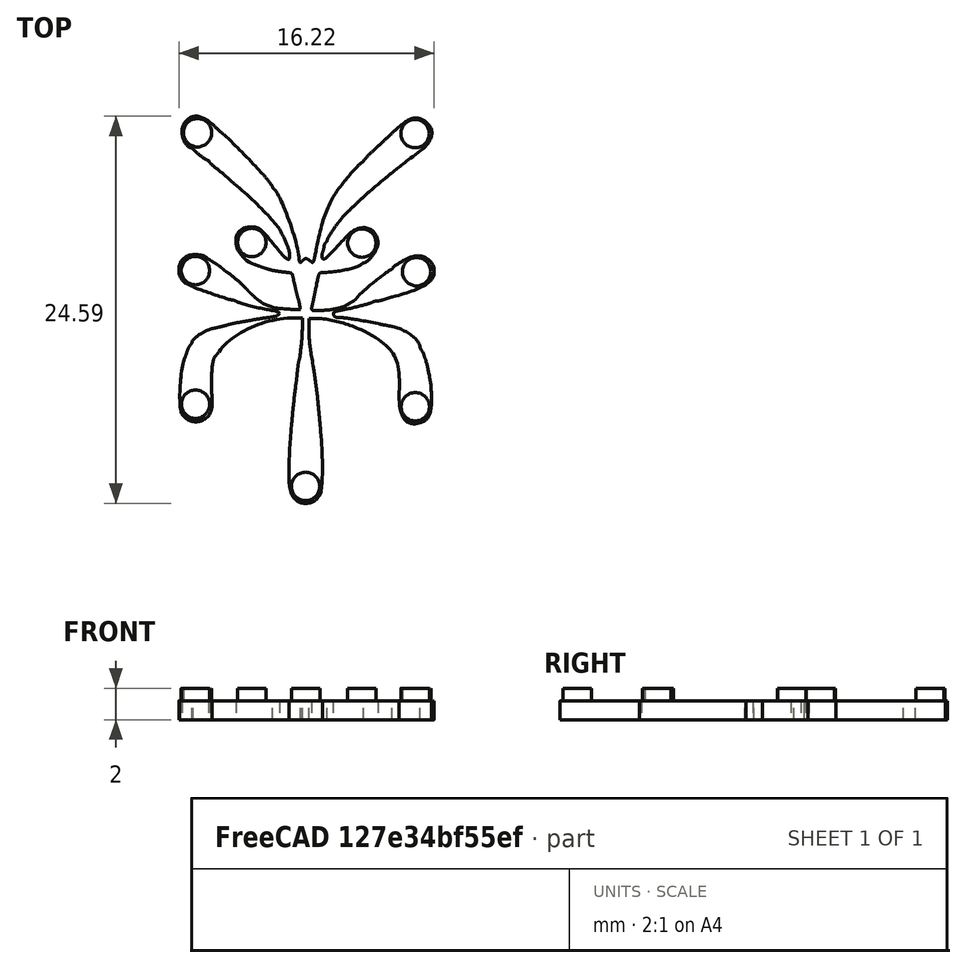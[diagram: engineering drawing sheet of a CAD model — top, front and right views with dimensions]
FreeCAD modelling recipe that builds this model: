
FCSTD DOCUMENT  (FreeCAD 0.20R29177 (Git))
Label: frexten
License: All rights reserved
LicenseURL: http://en.wikipedia.org/wiki/All_rights_reserved
objects: Part::FeaturePython×7, Sketcher::SketchObject×2, PartDesign::Pad×2, App::DocumentObjectGroupPython×2, Part::Feature×1, PartDesign::Body×1, App::MaterialObjectPython×1
note: 15 computed .brp shape members not serialized (recipe doc carries the construction recipe); baked Part::Feature solids carry a one-line shape summary decoded from their .brp

FEATURE [Part::Feature] path1527001
  shape: bbox 72.27 x 108.1 x 2e-07 mm, 1 faces, 0 solids (baked)
FEATURE [Part::FeaturePython] Clone  label="path1527002"  # Draft clone (typed FeaturePython)
  AttacherType = Attacher::AttachEngine3D
  Fuse = false
  Objects = -> [path1527001]
  Placement = pos=(26.6865,-58.6467,0) rot=(0,0,1;0rad)
  Scale = (0.23,0.23,0.23)
FEATURE [Sketcher::SketchObject] Sketch
  FullyConstrained = false
  sketch-geometry (125):
    g0: BSplineCurve PolesCount=4 KnotsCount=2 Degree=3 IsPeriodic=0
    g1: BSplineCurve PolesCount=4 KnotsCount=2 Degree=3 IsPeriodic=0
    g2: BSplineCurve PolesCount=4 KnotsCount=2 Degree=3 IsPeriodic=0
    g3: BSplineCurve PolesCount=4 KnotsCount=2 Degree=3 IsPeriodic=0
    g4: BSplineCurve PolesCount=4 KnotsCount=2 Degree=3 IsPeriodic=0
    g5: BSplineCurve PolesCount=4 KnotsCount=2 Degree=3 IsPeriodic=0
    g6: BSplineCurve PolesCount=2 KnotsCount=2 Degree=1 IsPeriodic=0
    g7: BSplineCurve PolesCount=2 KnotsCount=2 Degree=1 IsPeriodic=0
    g8: BSplineCurve PolesCount=4 KnotsCount=2 Degree=3 IsPeriodic=0
    g9: BSplineCurve PolesCount=4 KnotsCount=2 Degree=3 IsPeriodic=0
    g10: BSplineCurve PolesCount=4 KnotsCount=2 Degree=3 IsPeriodic=0
    g11: BSplineCurve PolesCount=4 KnotsCount=2 Degree=3 IsPeriodic=0
    g12: BSplineCurve PolesCount=4 KnotsCount=2 Degree=3 IsPeriodic=0
    g13: BSplineCurve PolesCount=4 KnotsCount=2 Degree=3 IsPeriodic=0
    g14: BSplineCurve PolesCount=4 KnotsCount=2 Degree=3 IsPeriodic=0
    g15: BSplineCurve PolesCount=4 KnotsCount=2 Degree=3 IsPeriodic=0
    g16: BSplineCurve PolesCount=4 KnotsCount=2 Degree=3 IsPeriodic=0
    g17: BSplineCurve PolesCount=4 KnotsCount=2 Degree=3 IsPeriodic=0
    g18: BSplineCurve PolesCount=4 KnotsCount=2 Degree=3 IsPeriodic=0
    g19: BSplineCurve PolesCount=4 KnotsCount=2 Degree=3 IsPeriodic=0
    g20: BSplineCurve PolesCount=4 KnotsCount=2 Degree=3 IsPeriodic=0
    g21: BSplineCurve PolesCount=4 KnotsCount=2 Degree=3 IsPeriodic=0
    g22: BSplineCurve PolesCount=4 KnotsCount=2 Degree=3 IsPeriodic=0
    g23: BSplineCurve PolesCount=4 KnotsCount=2 Degree=3 IsPeriodic=0
    g24: BSplineCurve PolesCount=4 KnotsCount=2 Degree=3 IsPeriodic=0
    g25: BSplineCurve PolesCount=4 KnotsCount=2 Degree=3 IsPeriodic=0
    g26: BSplineCurve PolesCount=4 KnotsCount=2 Degree=3 IsPeriodic=0
    g27: BSplineCurve PolesCount=4 KnotsCount=2 Degree=3 IsPeriodic=0
    g28: BSplineCurve PolesCount=4 KnotsCount=2 Degree=3 IsPeriodic=0
    g29: BSplineCurve PolesCount=4 KnotsCount=2 Degree=3 IsPeriodic=0
    g30: BSplineCurve PolesCount=4 KnotsCount=2 Degree=3 IsPeriodic=0
    g31: BSplineCurve PolesCount=4 KnotsCount=2 Degree=3 IsPeriodic=0
    g32: BSplineCurve PolesCount=4 KnotsCount=2 Degree=3 IsPeriodic=0
    g33: BSplineCurve PolesCount=4 KnotsCount=2 Degree=3 IsPeriodic=0
    g34: BSplineCurve PolesCount=4 KnotsCount=2 Degree=3 IsPeriodic=0
    g35: BSplineCurve PolesCount=4 KnotsCount=2 Degree=3 IsPeriodic=0
    g36: BSplineCurve PolesCount=4 KnotsCount=2 Degree=3 IsPeriodic=0
    g37: BSplineCurve PolesCount=4 KnotsCount=2 Degree=3 IsPeriodic=0
    g38: BSplineCurve PolesCount=4 KnotsCount=2 Degree=3 IsPeriodic=0
    g39: BSplineCurve PolesCount=4 KnotsCount=2 Degree=3 IsPeriodic=0
    g40: BSplineCurve PolesCount=4 KnotsCount=2 Degree=3 IsPeriodic=0
    g41: BSplineCurve PolesCount=4 KnotsCount=2 Degree=3 IsPeriodic=0
    g42: BSplineCurve PolesCount=4 KnotsCount=2 Degree=3 IsPeriodic=0
    g43: BSplineCurve PolesCount=4 KnotsCount=2 Degree=3 IsPeriodic=0
    g44: BSplineCurve PolesCount=4 KnotsCount=2 Degree=3 IsPeriodic=0
    g45: BSplineCurve PolesCount=4 KnotsCount=2 Degree=3 IsPeriodic=0
    g46: BSplineCurve PolesCount=4 KnotsCount=2 Degree=3 IsPeriodic=0
    g47: BSplineCurve PolesCount=4 KnotsCount=2 Degree=3 IsPeriodic=0
    g48: BSplineCurve PolesCount=4 KnotsCount=2 Degree=3 IsPeriodic=0
    g49: BSplineCurve PolesCount=4 KnotsCount=2 Degree=3 IsPeriodic=0
    g50: BSplineCurve PolesCount=4 KnotsCount=2 Degree=3 IsPeriodic=0
    g51: BSplineCurve PolesCount=4 KnotsCount=2 Degree=3 IsPeriodic=0
    g52: BSplineCurve PolesCount=4 KnotsCount=2 Degree=3 IsPeriodic=0
    g53: BSplineCurve PolesCount=4 KnotsCount=2 Degree=3 IsPeriodic=0
    g54: BSplineCurve PolesCount=4 KnotsCount=2 Degree=3 IsPeriodic=0
    g55: BSplineCurve PolesCount=4 KnotsCount=2 Degree=3 IsPeriodic=0
    g56: BSplineCurve PolesCount=4 KnotsCount=2 Degree=3 IsPeriodic=0
    g57: BSplineCurve PolesCount=4 KnotsCount=2 Degree=3 IsPeriodic=0
    g58: BSplineCurve PolesCount=4 KnotsCount=2 Degree=3 IsPeriodic=0
    g59: BSplineCurve PolesCount=4 KnotsCount=2 Degree=3 IsPeriodic=0
    g60: BSplineCurve PolesCount=4 KnotsCount=2 Degree=3 IsPeriodic=0
    g61: BSplineCurve PolesCount=4 KnotsCount=2 Degree=3 IsPeriodic=0
    g62: BSplineCurve PolesCount=4 KnotsCount=2 Degree=3 IsPeriodic=0
    g63: BSplineCurve PolesCount=4 KnotsCount=2 Degree=3 IsPeriodic=0
    g64: BSplineCurve PolesCount=4 KnotsCount=2 Degree=3 IsPeriodic=0
    g65: BSplineCurve PolesCount=4 KnotsCount=2 Degree=3 IsPeriodic=0
    g66: BSplineCurve PolesCount=4 KnotsCount=2 Degree=3 IsPeriodic=0
    g67: BSplineCurve PolesCount=4 KnotsCount=2 Degree=3 IsPeriodic=0
    g68: BSplineCurve PolesCount=4 KnotsCount=2 Degree=3 IsPeriodic=0
    g69: BSplineCurve PolesCount=4 KnotsCount=2 Degree=3 IsPeriodic=0
    g70: BSplineCurve PolesCount=4 KnotsCount=2 Degree=3 IsPeriodic=0
    g71: BSplineCurve PolesCount=4 KnotsCount=2 Degree=3 IsPeriodic=0
    g72: BSplineCurve PolesCount=4 KnotsCount=2 Degree=3 IsPeriodic=0
    g73: BSplineCurve PolesCount=4 KnotsCount=2 Degree=3 IsPeriodic=0
    g74: BSplineCurve PolesCount=4 KnotsCount=2 Degree=3 IsPeriodic=0
    g75: BSplineCurve PolesCount=4 KnotsCount=2 Degree=3 IsPeriodic=0
    g76: BSplineCurve PolesCount=4 KnotsCount=2 Degree=3 IsPeriodic=0
    g77: BSplineCurve PolesCount=4 KnotsCount=2 Degree=3 IsPeriodic=0
    g78: BSplineCurve PolesCount=4 KnotsCount=2 Degree=3 IsPeriodic=0
    g79: BSplineCurve PolesCount=4 KnotsCount=2 Degree=3 IsPeriodic=0
    g80: BSplineCurve PolesCount=4 KnotsCount=2 Degree=3 IsPeriodic=0
    g81: BSplineCurve PolesCount=4 KnotsCount=2 Degree=3 IsPeriodic=0
    g82: BSplineCurve PolesCount=4 KnotsCount=2 Degree=3 IsPeriodic=0
    g83: BSplineCurve PolesCount=4 KnotsCount=2 Degree=3 IsPeriodic=0
    g84: BSplineCurve PolesCount=4 KnotsCount=2 Degree=3 IsPeriodic=0
    g85: BSplineCurve PolesCount=4 KnotsCount=2 Degree=3 IsPeriodic=0
    g86: BSplineCurve PolesCount=4 KnotsCount=2 Degree=3 IsPeriodic=0
    g87: BSplineCurve PolesCount=2 KnotsCount=2 Degree=1 IsPeriodic=0
    g88: BSplineCurve PolesCount=2 KnotsCount=2 Degree=1 IsPeriodic=0
    g89: BSplineCurve PolesCount=4 KnotsCount=2 Degree=3 IsPeriodic=0
    g90: BSplineCurve PolesCount=4 KnotsCount=2 Degree=3 IsPeriodic=0
    g91: BSplineCurve PolesCount=4 KnotsCount=2 Degree=3 IsPeriodic=0
    g92: BSplineCurve PolesCount=4 KnotsCount=2 Degree=3 IsPeriodic=0
    g93: BSplineCurve PolesCount=4 KnotsCount=2 Degree=3 IsPeriodic=0
    g94: BSplineCurve PolesCount=4 KnotsCount=2 Degree=3 IsPeriodic=0
    g95: BSplineCurve PolesCount=4 KnotsCount=2 Degree=3 IsPeriodic=0
    g96: BSplineCurve PolesCount=4 KnotsCount=2 Degree=3 IsPeriodic=0
    g97: BSplineCurve PolesCount=4 KnotsCount=2 Degree=3 IsPeriodic=0
    g98: BSplineCurve PolesCount=4 KnotsCount=2 Degree=3 IsPeriodic=0
    g99: BSplineCurve PolesCount=4 KnotsCount=2 Degree=3 IsPeriodic=0
    g100: BSplineCurve PolesCount=4 KnotsCount=2 Degree=3 IsPeriodic=0
    g101: BSplineCurve PolesCount=4 KnotsCount=2 Degree=3 IsPeriodic=0
    g102: BSplineCurve PolesCount=4 KnotsCount=2 Degree=3 IsPeriodic=0
    g103: BSplineCurve PolesCount=4 KnotsCount=2 Degree=3 IsPeriodic=0
    g104: BSplineCurve PolesCount=4 KnotsCount=2 Degree=3 IsPeriodic=0
    g105: BSplineCurve PolesCount=4 KnotsCount=2 Degree=3 IsPeriodic=0
    g106: BSplineCurve PolesCount=4 KnotsCount=2 Degree=3 IsPeriodic=0
    g107: BSplineCurve PolesCount=4 KnotsCount=2 Degree=3 IsPeriodic=0
    g108: BSplineCurve PolesCount=4 KnotsCount=2 Degree=3 IsPeriodic=0
    g109: BSplineCurve PolesCount=4 KnotsCount=2 Degree=3 IsPeriodic=0
    g110: BSplineCurve PolesCount=4 KnotsCount=2 Degree=3 IsPeriodic=0
    g111: BSplineCurve PolesCount=4 KnotsCount=2 Degree=3 IsPeriodic=0
    g112: BSplineCurve PolesCount=4 KnotsCount=2 Degree=3 IsPeriodic=0
    g113: BSplineCurve PolesCount=4 KnotsCount=2 Degree=3 IsPeriodic=0
    g114: BSplineCurve PolesCount=4 KnotsCount=2 Degree=3 IsPeriodic=0
    g115: BSplineCurve PolesCount=4 KnotsCount=2 Degree=3 IsPeriodic=0
    g116: BSplineCurve PolesCount=4 KnotsCount=2 Degree=3 IsPeriodic=0
    g117: BSplineCurve PolesCount=2 KnotsCount=2 Degree=1 IsPeriodic=0
    g118: BSplineCurve PolesCount=2 KnotsCount=2 Degree=1 IsPeriodic=0
    g119: BSplineCurve PolesCount=4 KnotsCount=2 Degree=3 IsPeriodic=0
    g120: BSplineCurve PolesCount=4 KnotsCount=2 Degree=3 IsPeriodic=0
    g121: BSplineCurve PolesCount=4 KnotsCount=2 Degree=3 IsPeriodic=0
    g122: BSplineCurve PolesCount=4 KnotsCount=2 Degree=3 IsPeriodic=0
    g123: BSplineCurve PolesCount=4 KnotsCount=2 Degree=3 IsPeriodic=0
    g124: BSplineCurve PolesCount=4 KnotsCount=2 Degree=3 IsPeriodic=0
  constraints (125):
    c: Coincident(g0,g1)
    c: Coincident(g1,g2)
    c: Coincident(g2,g3)
    c: Coincident(g3,g4)
    c: Coincident(g4,g5)
    c: Coincident(g5,g6)
    c: Coincident(g6,g7)
    c: Coincident(g7,g8)
    c: Coincident(g8,g9)
    c: Coincident(g9,g10)
    c: Coincident(g10,g11)
    c: Coincident(g11,g12)
    c: Coincident(g12,g13)
    c: Coincident(g13,g14)
    c: Coincident(g14,g15)
    c: Coincident(g15,g16)
    c: Coincident(g16,g17)
    c: Coincident(g17,g18)
    c: Coincident(g18,g19)
    c: Coincident(g19,g20)
    c: Coincident(g20,g21)
    c: Coincident(g21,g22)
    c: Coincident(g22,g23)
    c: Coincident(g23,g24)
    c: Coincident(g24,g25)
    c: Coincident(g25,g26)
    c: Coincident(g26,g27)
    c: Coincident(g27,g28)
    c: Coincident(g28,g29)
    c: Coincident(g29,g30)
    c: Coincident(g30,g31)
    c: Coincident(g31,g32)
    c: Coincident(g32,g33)
    c: Coincident(g33,g34)
    c: Coincident(g34,g35)
    c: Coincident(g35,g36)
    c: Coincident(g36,g37)
    c: Coincident(g37,g38)
    c: Coincident(g38,g39)
    c: Coincident(g39,g40)
    c: Coincident(g40,g41)
    c: Coincident(g41,g42)
    c: Coincident(g42,g43)
    c: Coincident(g43,g44)
    c: Coincident(g44,g45)
    c: Coincident(g45,g46)
    c: Coincident(g46,g47)
    c: Coincident(g47,g48)
    c: Coincident(g48,g49)
    c: Coincident(g49,g50)
    c: Coincident(g50,g51)
    c: Coincident(g51,g52)
    c: Coincident(g52,g53)
    c: Coincident(g53,g54)
    c: Coincident(g54,g55)
    c: Coincident(g55,g56)
    c: Coincident(g56,g57)
    c: Coincident(g57,g58)
    c: Coincident(g58,g59)
    c: Coincident(g59,g60)
    c: Coincident(g60,g61)
    c: Coincident(g61,g62)
    c: Coincident(g62,g63)
    c: Coincident(g63,g64)
    c: Coincident(g64,g65)
    c: Coincident(g65,g66)
    c: Coincident(g66,g67)
    c: Coincident(g67,g68)
    c: Coincident(g68,g69)
    c: Coincident(g69,g70)
    c: Coincident(g70,g71)
    c: Coincident(g71,g72)
    c: Coincident(g72,g73)
    c: Coincident(g73,g74)
    c: Coincident(g74,g75)
    c: Coincident(g75,g76)
    c: Coincident(g76,g77)
    c: Coincident(g77,g78)
    c: Coincident(g78,g79)
    c: Coincident(g79,g80)
    c: Coincident(g80,g81)
    c: Coincident(g81,g82)
    c: Coincident(g82,g83)
    c: Coincident(g83,g84)
    c: Coincident(g84,g85)
    c: Coincident(g85,g86)
    c: Coincident(g86,g87)
    c: Coincident(g87,g88)
    c: Coincident(g88,g89)
    c: Coincident(g89,g90)
    c: Coincident(g90,g91)
    c: Coincident(g91,g92)
    c: Coincident(g92,g93)
    c: Coincident(g93,g94)
    c: Coincident(g94,g95)
    c: Coincident(g95,g96)
    c: Coincident(g96,g97)
    c: Coincident(g97,g98)
    c: Coincident(g98,g99)
    c: Coincident(g99,g100)
    c: Coincident(g100,g101)
    c: Coincident(g101,g102)
    c: Coincident(g102,g103)
    c: Coincident(g103,g104)
    c: Coincident(g104,g105)
    c: Coincident(g105,g106)
    c: Coincident(g106,g107)
    c: Coincident(g107,g108)
    c: Coincident(g108,g109)
    c: Coincident(g109,g110)
    c: Coincident(g110,g111)
    c: Coincident(g111,g112)
    c: Coincident(g112,g113)
    c: Coincident(g113,g114)
    c: Coincident(g114,g115)
    c: Coincident(g115,g116)
    c: Coincident(g116,g117)
    c: Coincident(g117,g118)
    c: Coincident(g118,g119)
    c: Coincident(g119,g120)
    c: Coincident(g120,g121)
    c: Coincident(g121,g122)
    c: Coincident(g122,g123)
    c: Coincident(g123,g124)
    c: Coincident(g124,g0)
FEATURE [PartDesign::Pad] Pad
  Direction = (0,0,1)
  Length = 1.2
  Length2 = 10
  Profile = -> Sketch
  ReferenceAxis = -> Sketch [N_Axis]
  Type = 0
FEATURE [Sketcher::SketchObject] Sketch001
  FullyConstrained = false
  MapMode = 5
  Support = -> [XY_Plane]
  sketch-geometry (9):
    g0: Circle CenterX=41.8068 CenterY=-64.4598 CenterZ=0 NormalX=0 NormalY=0 NormalZ=1 AngleXU=0 Radius=0.9
    g1: Circle CenterX=27.989 CenterY=-64.4045 CenterZ=0 NormalX=0 NormalY=0 NormalZ=1 AngleXU=0 Radius=0.9
    g2: Circle CenterX=38.4249 CenterY=-71.4153 CenterZ=0 NormalX=0 NormalY=0 NormalZ=1 AngleXU=0 Radius=0.9
    g3: Circle CenterX=31.4327 CenterY=-71.3736 CenterZ=0 NormalX=0 NormalY=0 NormalZ=1 AngleXU=0 Radius=0.9
    g4: Circle CenterX=27.8521 CenterY=-73.1631 CenterZ=0 NormalX=0 NormalY=0 NormalZ=1 AngleXU=0 Radius=0.9
    g5: Circle CenterX=41.9002 CenterY=-73.2312 CenterZ=0 NormalX=0 NormalY=0 NormalZ=1 AngleXU=0 Radius=0.9
    g6: Circle CenterX=41.815 CenterY=-81.8076 CenterZ=0 NormalX=0 NormalY=0 NormalZ=1 AngleXU=0 Radius=0.9
    g7: Circle CenterX=27.859 CenterY=-81.6485 CenterZ=0 NormalX=0 NormalY=0 NormalZ=1 AngleXU=0 Radius=0.9
    g8: Circle CenterX=34.8547 CenterY=-86.867 CenterZ=0 NormalX=0 NormalY=0 NormalZ=1 AngleXU=0 Radius=0.9
  constraints (9):
    c: Diameter(g8) = 1.8
    c: Diameter(g7) = 1.8
    c: Diameter(g6) = 1.8
    c: Diameter(g5) = 1.8
    c: Diameter(g4) = 1.8
    c: Diameter(g3) = 1.8
    c: Diameter(g2) = 1.8
    c: Diameter(g0) = 1.8
    c: Diameter(g1) = 1.8
FEATURE [PartDesign::Pad] Pad001
  BaseFeature = -> Pad
  Direction = (0,0,1)
  Length = 2
  Length2 = 10
  Profile = -> Sketch001
  ReferenceAxis = -> Sketch001 [N_Axis]
  Type = 0
FEATURE [PartDesign::Body] Body
  Group = -> [Sketch,Pad,Sketch001,Pad001]
  Origin = -> Origin
  Tip = -> Pad001
FEATURE [Part::FeaturePython] PhysicsModel  # WARN: FeaturePython — macro-defined, semantics opaque (R4)
  Flow = 0
  Phase = 0
  Thermal = 0
  Time = 0
  Turbulence = 3
  TurbulenceModel = 0
  gx = 0
  gy = -9800
  gz = 0
FEATURE [App::MaterialObjectPython] FluidProperties  # material (typed FeaturePython)
  Category = 1
  Material = CardName=AirIsothermal; Density=1.20 kg/m^3; Description=Standard air properties at 20 Degrees Celsius and 1 atm; DynamicViscosity=1.80e-5 kg/m/s; Name=Air; Type=Isothermal
FEATURE [Part::FeaturePython] InitialiseFields  # WARN: FeaturePython — macro-defined, semantics opaque (R4)
  PotentialFlow = true
  PotentialFlowP = false
  Pressure = 100
  ReThetat = 1
  Temperature = 290
  UseInletTemperatureValue = false
  UseInletTurbulenceValues = false
  UseInletUValues = false
  UseOutletPValue = false
  Ux = 0
  Uy = 0
  Uz = 0
  epsilon = 50000000
  gammaInt = 1
  k = 10000
  kEqnNut = 50000000
  kEqnk = 10000
  nuTilda = 55000000
  nut = 50000000
  omega = 57
FEATURE [Part::FeaturePython] CfdSolver  # WARN: FeaturePython — macro-defined, semantics opaque (R4)
  ConvergenceTol = 0.001
  EndTime = 1
  InputCaseName = case
  MaxIterations = 2000
  Parallel = true
  ParallelCores = 12
  SteadyWriteInterval = 50
  TimeStep = 0.001
  TransientWriteInterval = 0.1
FEATURE [Part::FeaturePython] CfdFluidBoundary  label="inlet"  # WARN: FeaturePython — macro-defined, semantics opaque (R4)
  BoundarySubType = 9
  BoundaryType = 1
  DefaultBoundary = false
  DirectionFace = CfdFluidBoundary:Face1
  DissipationRate = 50000000
  HeatFlux = 0
  HeatTransferCoeff = 0
  Intermittency = 1
  MassFlowRate = 0
  NuTilda = 55000000
  PorousBaffleMethod = 0
  Pressure = 100
  PressureDropCoeff = 0
  ReThetat = 1
  ReverseNormal = false
  ScreenSpacing = 2
  ScreenWireDiameter = 0.2
  ShapeRefs = -> [Pad001]
  SlipRatio = 0
  SpecificDissipationRate = 57
  Temperature = 290
  ThermalBoundaryType = 0
  TurbulenceInletSpecification = 5
  TurbulenceIntensityPercentage = 1
  TurbulenceLengthScale = 100
  TurbulentKineticEnergy = 10000
  TurbulentViscosity = 50000000
  Ux = 0
  Uy = 0
  Uz = 0
  VelocityIsCartesian = false
  VelocityMag = 100
  VolFlowRate = 0
  kEqnTurbulentKineticEnergy = 10000
  kEqnTurbulentViscosity = 50000000
FEATURE [Part::FeaturePython] CfdFluidBoundary001  label="outlet"  # WARN: FeaturePython — macro-defined, semantics opaque (R4)
  BoundarySubType = 10
  BoundaryType = 2
  DefaultBoundary = false
  DissipationRate = 50000000
  HeatFlux = 0
  HeatTransferCoeff = 0
  Intermittency = 1
  MassFlowRate = 0
  NuTilda = 55000000
  PorousBaffleMethod = 0
  Pressure = 0
  PressureDropCoeff = 0
  ReThetat = 1
  ReverseNormal = false
  ScreenSpacing = 2
  ScreenWireDiameter = 0.2
  ShapeRefs = -> [Pad001]
  SlipRatio = 0
  SpecificDissipationRate = 57
  Temperature = 290
  ThermalBoundaryType = 0
  TurbulenceInletSpecification = 5
  TurbulenceIntensityPercentage = 1
  TurbulenceLengthScale = 100
  TurbulentKineticEnergy = 10000
  TurbulentViscosity = 50000000
  Ux = 0
  Uy = 0
  Uz = 0
  VelocityIsCartesian = true
  VelocityMag = 0
  VolFlowRate = 0
  kEqnTurbulentKineticEnergy = 10000
  kEqnTurbulentViscosity = 50000000
FEATURE [Part::FeaturePython] CfdFluidBoundary002  label="wall"  # WARN: FeaturePython — macro-defined, semantics opaque (R4)
  BoundarySubType = 0
  BoundaryType = 0
  DefaultBoundary = false
  DissipationRate = 50000000
  HeatFlux = 0
  HeatTransferCoeff = 0
  Intermittency = 1
  MassFlowRate = 0
  NuTilda = 55000000
  PorousBaffleMethod = 0
  Pressure = 0
  PressureDropCoeff = 0
  ReThetat = 1
  ReverseNormal = false
  ScreenSpacing = 2
  ScreenWireDiameter = 0.2
  ShapeRefs = -> [Pad001]
  SlipRatio = 0
  SpecificDissipationRate = 57
  Temperature = 290
  ThermalBoundaryType = 0
  TurbulenceInletSpecification = 5
  TurbulenceIntensityPercentage = 1
  TurbulenceLengthScale = 100
  TurbulentKineticEnergy = 10000
  TurbulentViscosity = 50000000
  Ux = 0
  Uy = 0
  Uz = 0
  VelocityIsCartesian = true
  VelocityMag = 0
  VolFlowRate = 0
  kEqnTurbulentKineticEnergy = 10000
  kEqnTurbulentViscosity = 50000000
FEATURE [App::DocumentObjectGroupPython] Pad001_Mesh  # scripted group (container) (typed FeaturePython)
  CaseName = meshCase
  CellsBetweenLevels = 3
  CharacteristicLengthMax = 0.05
  ConvertToDualMesh = false
  EdgeRefinement = 1
  ElementDimension = 1
  ImplicitEdgeDetection = false
  MeshUtility = 0
  NumberOfProcesses = 1
  NumberOfThreads = 0
  Part = -> Pad001
  PointInMesh = x=0 m; y=0 m; z=0 m
  STLAngularMeshDensity = 100
  STLRelativeLinearDeflection = 0.001
FEATURE [App::DocumentObjectGroupPython] CfdAnalysis  # scripted group (container) (typed FeaturePython)
  Group = -> [PhysicsModel,FluidProperties,InitialiseFields,CfdSolver,CfdFluidBoundary,CfdFluidBoundary001,CfdFluidBoundary002,Pad001_Mesh]
  IsActiveAnalysis = true
  NeedsCaseRewrite = false
  NeedsMeshRerun = true
  NeedsMeshRewrite = true
